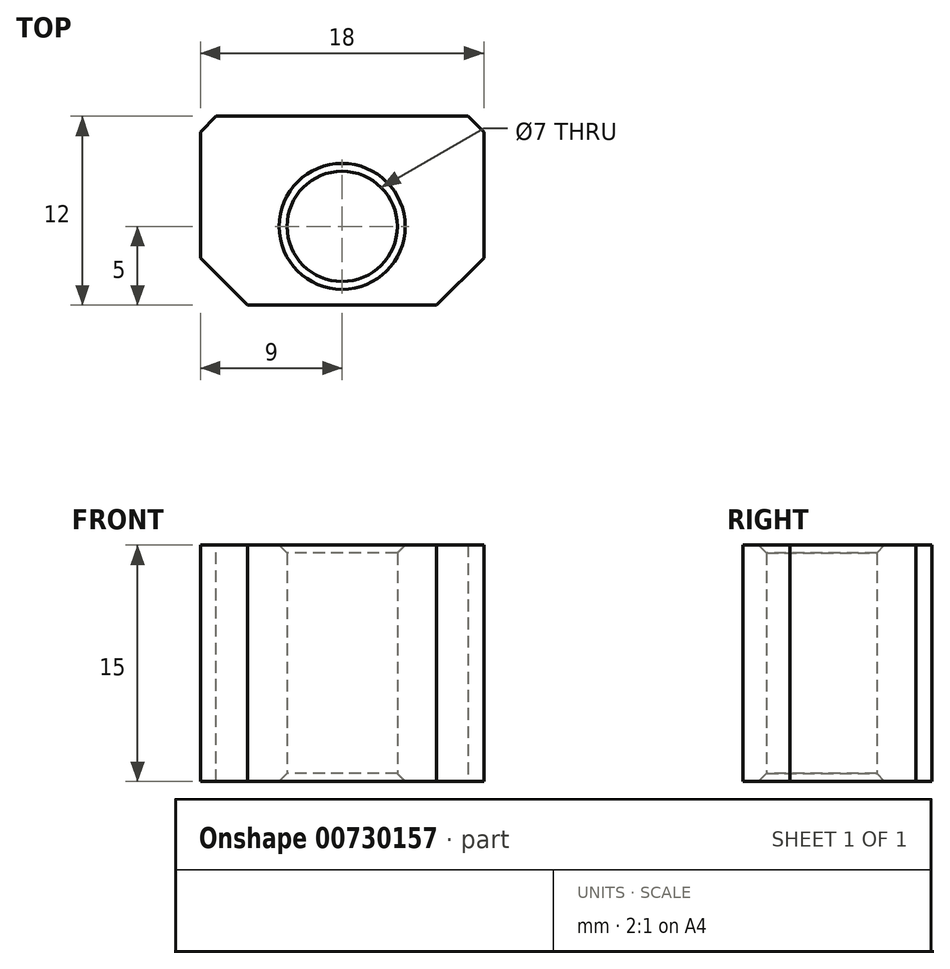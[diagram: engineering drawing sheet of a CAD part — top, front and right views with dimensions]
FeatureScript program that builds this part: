
annotation { "Feature Type Name" : "Feature", "Feature Type Description" : "" }
export const myFeature = defineFeature(function(context is Context, id is Id, definition is map)
    precondition{}
    {
        {
            var Q0;
            Q0=qCreatedBy(makeId("Top.planeOp"),FACE);
            var sketch = newSketch(context, id + "F0", { "sketchPlane" : qUnion([Q0])});
            skLineSegment(sketch, "E0.bottom", {"start": v(9, 6) * mm, "end": v(-9, 6) * mm});
            skLineSegment(sketch, "E0.top", {"start": v(9, -6) * mm, "end": v(-9, -6) * mm});
            skLineSegment(sketch, "E0.left", {"start": v(9, 6) * mm, "end": v(9, -6) * mm});
            skLineSegment(sketch, "E0.right", {"start": v(-9, 6) * mm, "end": v(-9, -6) * mm});
            skPoint(sketch, "E0.middle", {"position": v(0, 0) * mm});
            skCircle(sketch, "E1", {"center": v(0, -1) * mm, "radius": 3.5 * mm});
            skSolve(sketch);
        }
        {
            var Q0;
            Q0=makeQuery(id+"F0.imprint","IMPRINT",FACE,{"disambiguationData":[TD([[makeQuery(id+"F0.imprint","IMPRINT",EDGE,{"derivedFrom":sQuery(id+"F0.wireOp",EDGE,"E0.bottom")}),1.0]])]});
            extrude(context, id + "F1", {"entities" : qUnion([Q0]), "depth" : 15 * mm, "offsetDistance" : 25 * mm});
        }
        {
            var Q0;
            Q0=makeQuery(id+"F1.opExtrude","SWEPT_EDGE",EDGE,{"disambiguationData":[OSD([sQuery(id+"F0.wireOp",EDGE,"E0.top"),sQuery(id+"F0.wireOp",EDGE,"E0.left")])]});
            var Q1;
            Q1=makeQuery(id+"F1.opExtrude","SWEPT_EDGE",EDGE,{"disambiguationData":[OSD([sQuery(id+"F0.wireOp",EDGE,"E0.top"),sQuery(id+"F0.wireOp",EDGE,"E0.right")])]});
            chamfer(context, id + "F2", {"entities" : qUnion([Q0, Q1]), "width" : 3 * mm, "tangentPropagation" : true});
        }
        {
            var Q0;
            Q0=makeQuery(id+"F1.opExtrude","SWEPT_EDGE",EDGE,{"disambiguationData":[OSD([sQuery(id+"F0.wireOp",EDGE,"E0.bottom"),sQuery(id+"F0.wireOp",EDGE,"E0.left")])]});
            var Q1;
            Q1=makeQuery(id+"F1.opExtrude","SWEPT_EDGE",EDGE,{"disambiguationData":[OSD([sQuery(id+"F0.wireOp",EDGE,"E0.bottom"),sQuery(id+"F0.wireOp",EDGE,"E0.right")])]});
            chamfer(context, id + "F3", {"entities" : qUnion([Q0, Q1]), "width" : 1 * mm, "tangentPropagation" : true});
        }
        {
            var Q0;
            Q0=makeQuery(id+"F1.opExtrude","CAP_EDGE",EDGE,{"disambiguationData":[OSD([sQuery(id+"F0.wireOp",EDGE,"E1")])],"isStart":true});
            var Q1;
            Q1=makeQuery(id+"F1.opExtrude","CAP_EDGE",EDGE,{"disambiguationData":[OSD([sQuery(id+"F0.wireOp",EDGE,"E1")])],"isStart":false});
            chamfer(context, id + "F4", {"entities" : qUnion([Q0, Q1]), "width" : .5 * mm, "tangentPropagation" : true});
        }
    });
